# Revit family: xxxFaucet-Kitchen-Grohe-Essence_New-31616_Series
name_source: partatom
category: Plumbing Fixtures
units: mm (PartAtom-declared; Revit-internal decimal feet)

## family parameters
Always vertical = No
Cut with Voids When Loaded = No
OmniClass Number = 23.45.55.14
OmniClass Title = Single Faucets
Part Type = Normal
Room Calculation Point = No
Round Connector Dimension = Use Diameter
Shared = Yes
Work Plane-Based = Yes

## types (2) — shared parameters
Assembly Code = D2020300
CW Connection = No
CWFU = 1.5
Compliance Certifications = CEC Certified, Low Lead Certified, CALGreen Compliant, Energy Policy Act of 1992, NSF 61, NSF 372, CSA B125.1, ASME A112.18.1 & Complies with lead plumbing laws
Default Elevation = 0"
Description = SmartControl Pull-out Single Spray Kitchen Faucet 1.75 GPM
Flow Rate = 1.75 gpm (6.6 L/min)
HW Connection = No
HWFU = 1.5
Height = 14 7/16"
Height- Spout = 12 3/8"
Installation Instruction Link = https://americanstandard.box.com
Installation Type = Deck-Mounted
Length- Spout Reach = 7 13/16"
Manufacturer = Grohe
Max. Hot Water Temp. = 158 °F
Min Max. Operating Pressure = 7.25 psi - 145 psi
Price = Prices may vary. Please consult Manufacturer Representative for most up-to-date price list.
Product Documentation Link = https://americanstandard.box.com
Product Page URL = https://www.grohe.us
Revised Date = 03/02/2022
Tempered Water Connection = Yes
Tempered Water Connection Diameter = 3/8"
URL = https://www.grohe.us
Vent Connection = No
WFU = 2
Waste Connection = No

## per-type parameters (varying)
| type | Finish | Material |
| 31616000 | Metal-Grohe-000-Starlight Chrome | Metal-Grohe-000-Starlight Chrome |
| 31616DC0 | Metal-Grohe-DC0-SuperSteel Infinity Finish | Metal-Grohe-DC0-SuperSteel Infinity Finish |

note: column(s) folded — value = type name in every type: Model

## geometry (parser evidence)
native form markers: Sweep x2
no freeform markers — native parametric forms only
